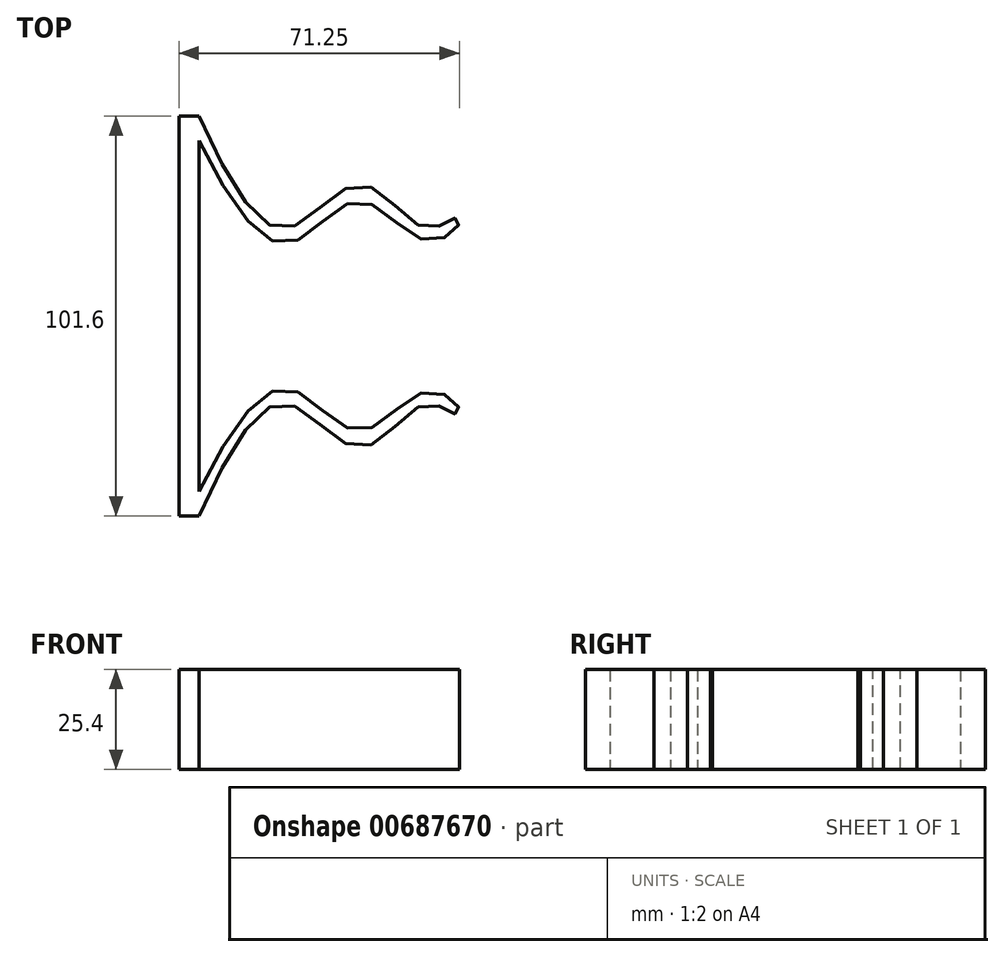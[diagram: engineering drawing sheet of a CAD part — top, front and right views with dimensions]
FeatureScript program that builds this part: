
annotation { "Feature Type Name" : "Feature", "Feature Type Description" : "" }
export const myFeature = defineFeature(function(context is Context, id is Id, definition is map)
    precondition{}
    {
        {
            var Q0;
            Q0=qCreatedBy(makeId("Top.planeOp"),FACE);
            var sketch = newSketch(context, id + "F0", { "sketchPlane" : qUnion([Q0])});
            skLineSegment(sketch, "E0", {"start": v(0, 0) * mm, "end": v(0, 50.8) * mm});
            skLineSegment(sketch, "E1", {"start": v(0, 50.8) * mm, "end": v(5.08, 50.8) * mm});
            skLineSegment(sketch, "E2", {"start": v(5.08, 50.8) * mm, "end": v(5.08, 0) * mm});
            skLineSegment(sketch, "E3", {"start": v(5.08, 0) * mm, "end": v(0, 0) * mm});
            skFitSpline(sketch, "E4", {"points": [v(5.08, 50.8) * mm, v(27.55, 22.36) * mm, v(46.26, 33.42) * mm, v(62.77, 22.36) * mm, v(70.39, 24.9) * mm, v(71.18, 23.47) * mm, v(62.77, 19.19) * mm, v(45.64, 29.18) * mm, v(27.87, 18.55) * mm, v(5.08, 44.52) * mm], "startDerivative": vector(132.5, -295.98) * mm, "endDerivative": vector(-139.43, 275.36) * mm});
            skFitSpline(sketch, "E5.MirrorCS", {"points": [v(5.08, -50.8) * mm, v(27.55, -22.36) * mm, v(46.26, -33.42) * mm, v(62.77, -22.36) * mm, v(70.39, -24.9) * mm, v(71.18, -23.47) * mm, v(62.77, -19.19) * mm, v(45.64, -29.18) * mm, v(27.87, -18.55) * mm, v(5.08, -44.52) * mm], "startDerivative": vector(132.5, 295.98) * mm, "endDerivative": vector(-139.43, -275.36) * mm});
            skLineSegment(sketch, "E6.MirrorCS", {"start": v(5.08, -50.8) * mm, "end": v(5.08, 0) * mm});
            skLineSegment(sketch, "E7.MirrorCS", {"start": v(0, 0) * mm, "end": v(0, -50.8) * mm});
            skLineSegment(sketch, "E8.MirrorCS", {"start": v(0, -50.8) * mm, "end": v(5.08, -50.8) * mm});
            skSolve(sketch);
        }
        {
            var Q0;
            {var subQ0=sQuery(id+"F0.wireOp",EDGE,"E5.MirrorCS");Q0=makeQuery(id+"F0.imprint","IMPRINT",FACE,{"disambiguationData":[TD([[makeQuery(id+"F0.imprint","IMPRINT",EDGE,{"derivedFrom":subQ0}),1.0]])]});}
            var Q1;
            {var subQ1=sQuery(id+"F0.wireOp",EDGE,"E3");Q1=makeQuery(id+"F0.imprint","IMPRINT",FACE,{"disambiguationData":[TD([[makeQuery(id+"F0.imprint","IMPRINT",EDGE,{"derivedFrom":subQ1}),1.0]])]});}
            var Q2;
            Q2=makeQuery(id+"F0.imprint","IMPRINT",FACE,{"disambiguationData":[TD([[makeQuery(id+"F0.imprint","IMPRINT",EDGE,{"derivedFrom":sQuery(id+"F0.wireOp",EDGE,"E0")}),-1.0]])]});
            var Q3;
            {var subQ0=sQuery(id+"F0.wireOp",EDGE,"E4");Q3=makeQuery(id+"F0.imprint","IMPRINT",FACE,{"disambiguationData":[TD([[makeQuery(id+"F0.imprint","IMPRINT",EDGE,{"derivedFrom":subQ0}),-1.0]])]});}
            extrude(context, id + "F1", {"entities" : qUnion([Q0, Q1, Q2, Q3]), "depth" : 25.4 * mm, "offsetDistance" : 25.4 * mm});
        }
    });
